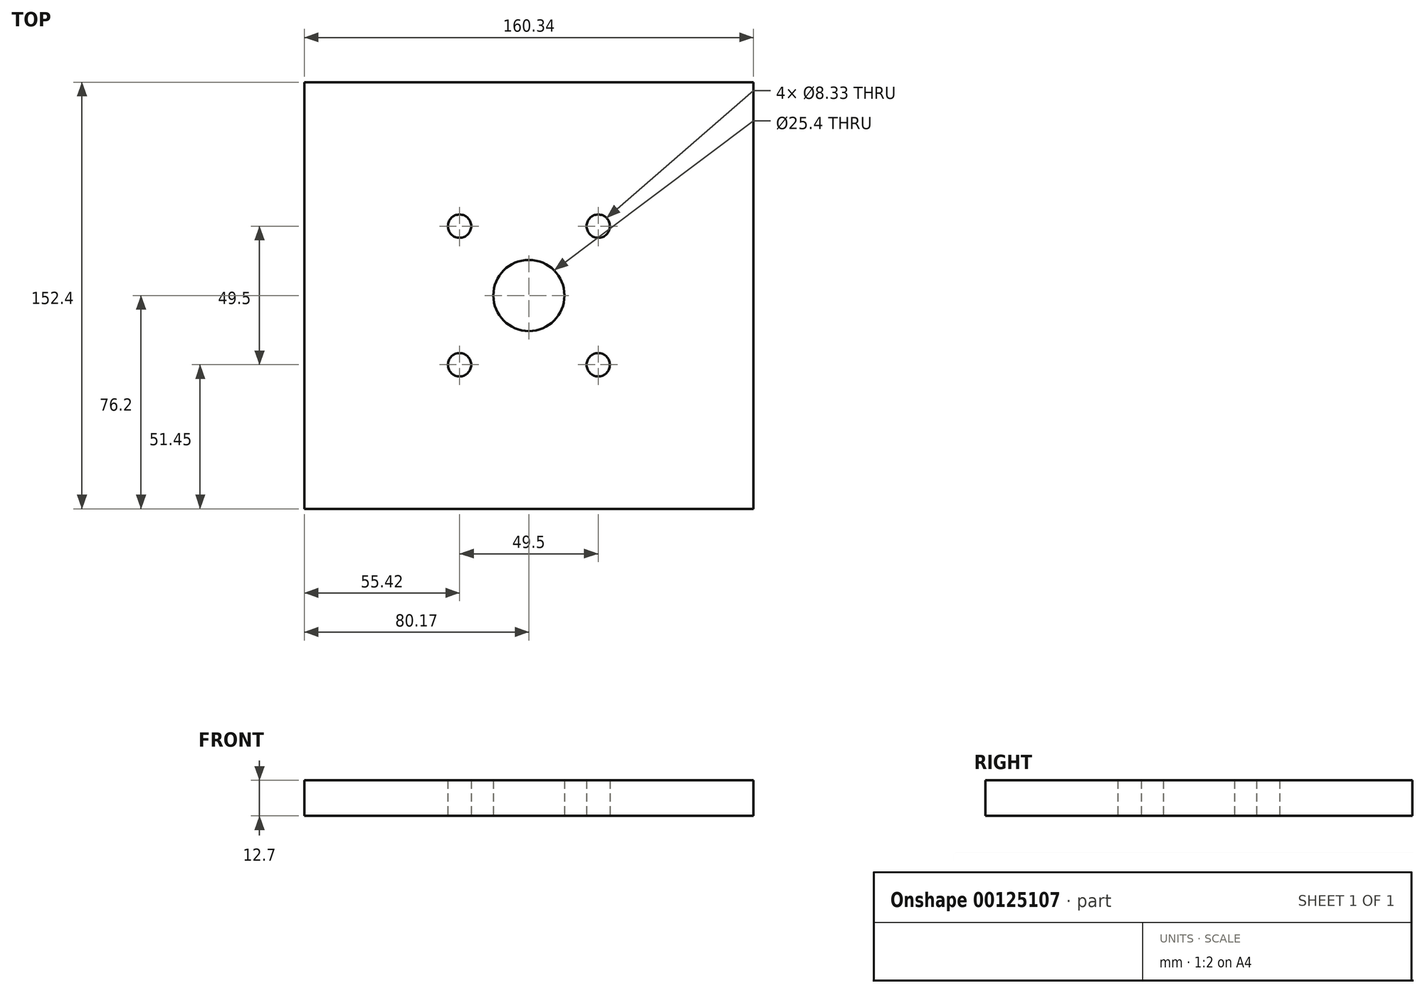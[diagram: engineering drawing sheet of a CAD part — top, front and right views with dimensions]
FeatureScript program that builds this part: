
annotation { "Feature Type Name" : "Feature", "Feature Type Description" : "" }
export const myFeature = defineFeature(function(context is Context, id is Id, definition is map)
    precondition{}
    {
        {
            var Q0;
            Q0=qCreatedBy(makeId("Top.planeOp"),FACE);
            var sketch = newSketch(context, id + "F0", { "sketchPlane" : qUnion([Q0])});
            skLineSegment(sketch, "E0.bottom", {"start": v(-80.17, -76.2) * mm, "end": v(80.17, -76.2) * mm});
            skLineSegment(sketch, "E0.top", {"start": v(-80.17, 76.2) * mm, "end": v(80.17, 76.2) * mm});
            skLineSegment(sketch, "E0.left", {"start": v(-80.17, -76.2) * mm, "end": v(-80.17, 76.2) * mm});
            skLineSegment(sketch, "E0.right", {"start": v(80.17, -76.2) * mm, "end": v(80.17, 76.2) * mm});
            skPoint(sketch, "E0.middle", {"position": v(0, 0) * mm});
            skCircle(sketch, "E1", {"center": v(0, 0) * mm, "radius": 12.7 * mm});
            skCircle(sketch, "E2", {"center": v(-24.75, -24.75) * mm, "radius": 4.17 * mm});
            skCircle(sketch, "E3.MirrorC", {"center": v(24.75, -24.75) * mm, "radius": 4.17 * mm});
            skCircle(sketch, "E4.MirrorC", {"center": v(-24.75, 24.75) * mm, "radius": 4.17 * mm});
            skCircle(sketch, "E5.MirrorC", {"center": v(24.75, 24.75) * mm, "radius": 4.17 * mm});
            skSolve(sketch);
        }
        {
            var Q0;
            Q0=makeQuery(id+"F0.imprint","IMPRINT",FACE,{"disambiguationData":[TD([[makeQuery(id+"F0.imprint","IMPRINT",EDGE,{"derivedFrom":sQuery(id+"F0.wireOp",EDGE,"E0.bottom")}),1.0]])]});
            extrude(context, id + "F1", {"entities" : qUnion([Q0]), "depth" : 12.7 * mm});
        }
    });
